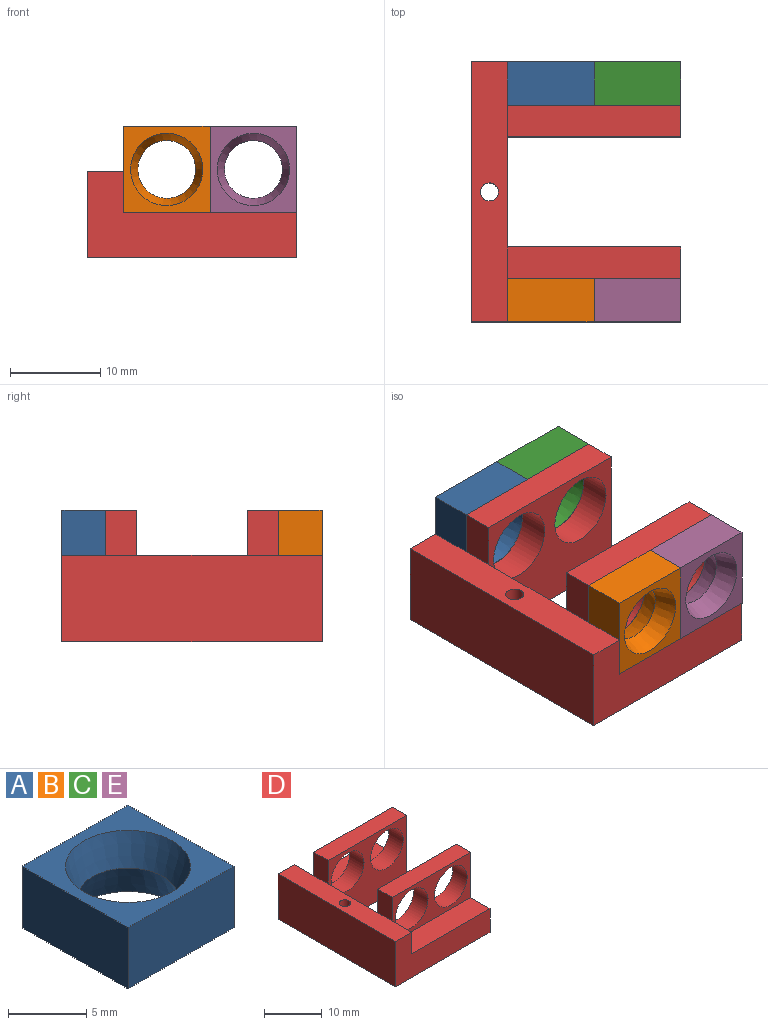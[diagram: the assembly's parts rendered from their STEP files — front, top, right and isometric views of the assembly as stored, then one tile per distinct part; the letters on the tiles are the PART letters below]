
ASSEMBLY  parts=5 mates=4
PART A: 8 faces, bbox 9.6x9.6x4.8 mm
  f0: plane 9.6x9.6mm, normal (0,0,1), area 41.9mm2, adj f2,f4,f5,f6,f7
  f1: plane 9.6x9.6mm, normal (0,0,-1), area 41.9mm2, adj f3,f4,f5,f6,f7
  f2: cone r=3.2mm half-angle=18.4deg, axis (0,0,1), area 57.2mm2, adj f0,f3
  f3: cone r=4mm half-angle=18.4deg, axis (0,0,-1), area 57.2mm2, adj f1,f2
  f4: plane 9.6x4.8mm, normal (0,1,0), area 46.1mm2, adj f0,f1,f5,f6
  f5: plane 9.6x4.8mm, normal (1,0,0), area 46.1mm2, adj f0,f1,f4,f7
  f6: plane 9.6x4.8mm, normal (-1,0,0), area 46.1mm2, adj f0,f1,f4,f7
  f7: plane 9.6x4.8mm, normal (0,-1,0), area 46.1mm2, adj f0,f1,f5,f6
PART B: same geometry as A
PART C: same geometry as A
PART D: 25 faces, bbox 23.2x28.8x14.6 mm
  f0: plane 4.8x4.6mm, normal (1,0,0), area 22.1mm2, adj f3,f7,f15,f23
  f1: plane 12.2x9.6mm, normal (1,0,0), area 117.1mm2, adj f7,f8,f11,f16
  f2: plane 4.8x4.6mm, normal (1,0,0), area 22.1mm2, adj f5,f7,f12,f24
  f3: plane 23.2x9.6mm, normal (0,1,0), area 134.4mm2, adj f0,f4,f7,f8,f17,f23
  f4: plane 28.8x9.6mm, normal (-1,0,0), area 276.5mm2, adj f3,f5,f7,f8
  f5: plane 23.2x9.6mm, normal (0,-1,0), area 134.4mm2, adj f2,f4,f7,f8,f10,f24
  f6: cylinder r=1mm len=9.6mm, axis (0,0,-1), area 60.3mm2, adj f7,f8
  f7: plane 28.8x4mm, normal (0,0,1), area 112.1mm2, adj f0,f1,f2,f3,f4,f5,f6,f9
  f8: plane 28.8x23.2mm, normal (0,0,-1), area 430.8mm2, adj f1,f3,f4,f5,f6,f10,f11,f16
  f9: plane 5x3.5mm, normal (-1,0,0), area 17.5mm2, adj f7,f11,f12,f13
  f10: plane 14.6x8.3mm, normal (1,0,0), area 75.1mm2, adj f5,f8,f11,f12,f13,f24
  f11: plane 19.2x14.6mm, normal (0,1,0), area 179.8mm2, adj f1,f8,f9,f10,f13,f21,f22
  f12: plane 19.2x9.6mm, normal (0,-1,0), area 83.8mm2, adj f2,f9,f10,f13,f21,f22,f24
  f13: plane 19.2x3.5mm, normal (0,0,1), area 67.2mm2, adj f9,f10,f11,f12
  f14: plane 5x3.5mm, normal (-1,0,0), area 17.5mm2, adj f7,f15,f16,f18
  f15: plane 19.2x9.6mm, normal (0,1,0), area 83.8mm2, adj f0,f14,f17,f18,f19,f20,f23
  f16: plane 19.2x14.6mm, normal (0,-1,0), area 179.8mm2, adj f1,f8,f14,f17,f18,f19,f20
  f17: plane 14.6x8.3mm, normal (1,0,0), area 75.1mm2, adj f3,f8,f15,f16,f18,f23
  f18: plane 19.2x3.5mm, normal (0,0,1), area 67.2mm2, adj f14,f15,f16,f17
  f19: cylinder r=4mm len=8mm, axis (0,-1,0), area 88mm2, adj f15,f16
  f20: cylinder r=4mm len=8mm, axis (0,-1,0), area 88mm2, adj f15,f16
  f21: cylinder r=4mm len=8mm, axis (0,-1,0), area 88mm2, adj f11,f12
  f22: cylinder r=4mm len=8mm, axis (0,-1,0), area 88mm2, adj f11,f12
  f23: plane 19.2x4.8mm, normal (0,0,1), area 92.2mm2, adj f0,f3,f15,f17
  f24: plane 19.2x4.8mm, normal (0,0,1), area 92.2mm2, adj f2,f5,f10,f12
PART E: same geometry as A
PLACE A rot(axis=(-1,0,0),90deg) t=(-6.17,6.14,22.33)mm
PLACE B rot(axis=(-1,0,0),90deg) t=(-6.17,-17.86,22.33)mm
PLACE C rot(axis=(1,0,0),90deg) t=(3.43,10.94,-9.67)mm
PLACE D t=(-1.37,-3.46,-3.47)mm
PLACE E rot(axis=(-1,0,0),90deg) t=(3.43,-17.86,22.33)mm
MATE fastened E.f2 <-> D.f19  axis (0,1,0) through (3.43,-13.06,6.33)mm
MATE fastened C.f2 <-> D.f19  axis (0,-1,0) through (3.43,6.14,6.33)mm
MATE fastened A.f2 <-> D.f20  axis (0,-1,0) through (-6.17,6.14,6.33)mm
MATE fastened B.f2 <-> D.f20  axis (0,1,0) through (-6.17,-13.06,6.33)mm
